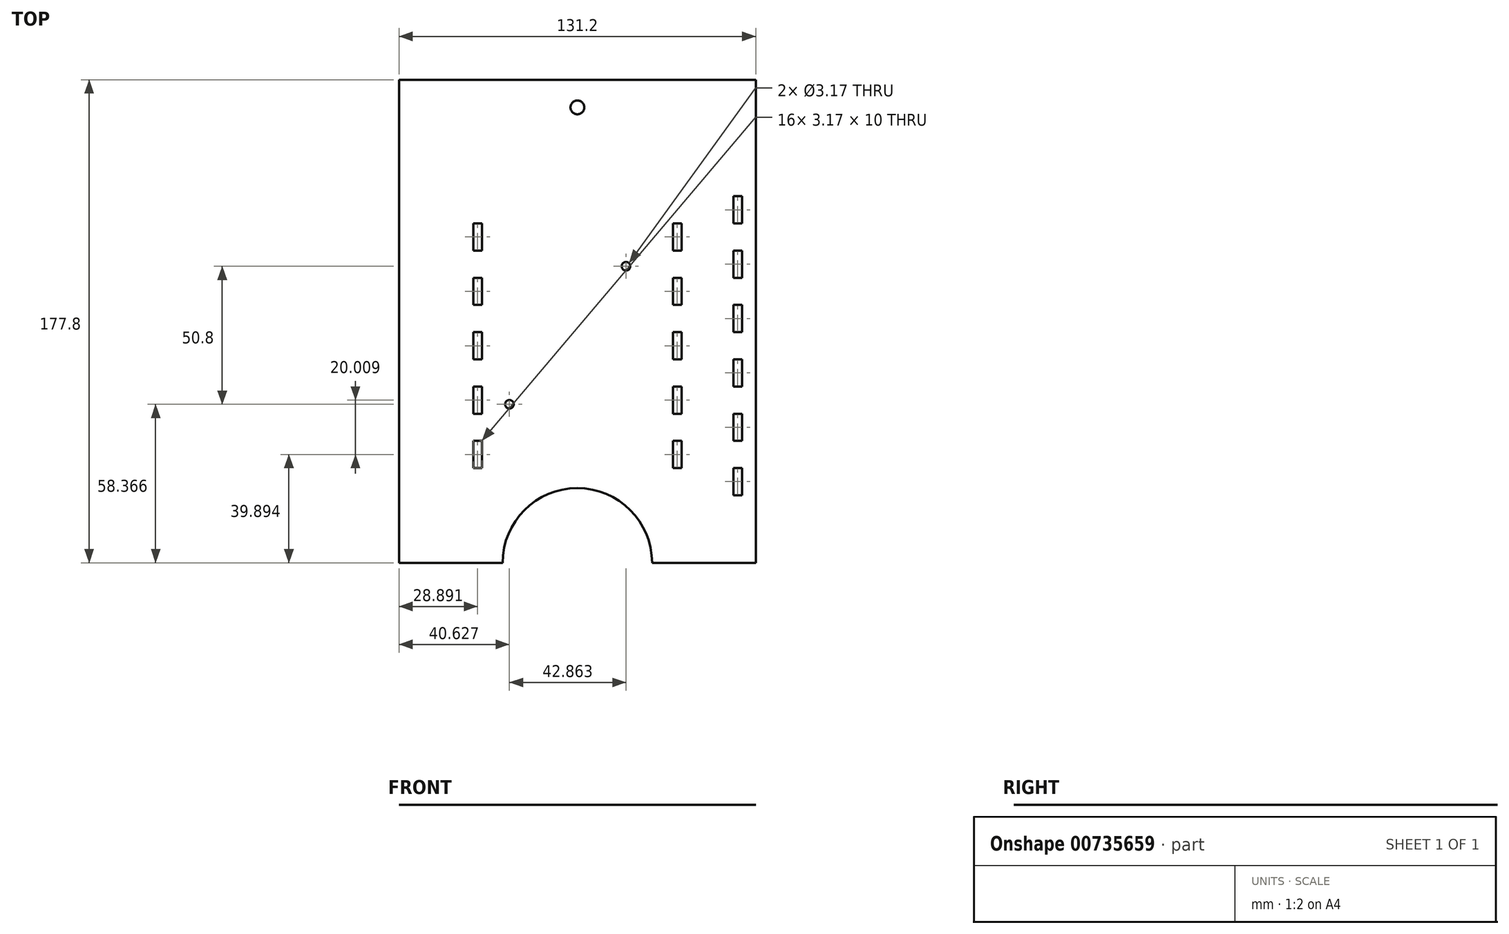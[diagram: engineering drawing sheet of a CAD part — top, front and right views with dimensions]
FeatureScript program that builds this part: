
annotation { "Feature Type Name" : "Feature", "Feature Type Description" : "" }
export const myFeature = defineFeature(function(context is Context, id is Id, definition is map)
    precondition{}
    {
        {
            var Q0;
            Q0=qCreatedBy(makeId("Top.planeOp"),FACE);
            var sketch = newSketch(context, id + "F0", { "sketchPlane" : qUnion([Q0])});
            skLineSegment(sketch, "E0.top", {"start": v(-188.86, -74.91) * mm, "end": v(-226.96, -74.91) * mm});
            skLineSegment(sketch, "E1.MirrorCS", {"start": v(-133.86, -74.91) * mm, "end": v(-95.76, -74.91) * mm});
            skCircle(sketch, "E2", {"center": v(-161.36, 92.73) * mm, "radius": 2.54 * mm});
            skLineSegment(sketch, "E3", {"start": v(-226.96, 102.89) * mm, "end": v(-95.76, 102.89) * mm});
            skArc(sketch, "E4", {"start": v(-133.86, -74.91) * mm, "mid": v(-161.36, -47.41) * mm, "end": v(-188.86, -74.91) * mm});
            skLineSegment(sketch, "E5", {"start": v(-226.96, 102.89) * mm, "end": v(-226.96, -74.91) * mm});
            skLineSegment(sketch, "E6", {"start": v(-95.76, 102.89) * mm, "end": v(-95.76, -74.91) * mm});
            skPoint(sketch, "E7", {"position": v(-221.88, 60.03) * mm});
            skPoint(sketch, "E8", {"position": v(-196.48, 60.03) * mm});
            skLineSegment(sketch, "E9.bottom", {"start": v(-221.88, 60.03) * mm, "end": v(-218.7, 60.03) * mm});
            skLineSegment(sketch, "E9.top", {"start": v(-221.88, -50.02) * mm, "end": v(-218.7, -50.02) * mm});
            skLineSegment(sketch, "E9.left", {"start": v(-221.88, 60.03) * mm, "end": v(-221.88, -50.02) * mm});
            skLineSegment(sketch, "E9.right", {"start": v(-218.7, 60.03) * mm, "end": v(-218.7, -50.02) * mm});
            skLineSegment(sketch, "E10.bottom", {"start": v(-196.48, 60.03) * mm, "end": v(-199.66, 60.03) * mm});
            skLineSegment(sketch, "E10.top", {"start": v(-196.48, -50.02) * mm, "end": v(-199.66, -50.02) * mm});
            skLineSegment(sketch, "E10.left", {"start": v(-196.48, 60.03) * mm, "end": v(-196.48, -50.02) * mm});
            skLineSegment(sketch, "E10.right", {"start": v(-199.66, 60.03) * mm, "end": v(-199.66, -50.02) * mm});
            skLineSegment(sketch, "E11.top", {"start": v(-221.88, 50.02) * mm, "end": v(-218.7, 50.02) * mm});
            skLineSegment(sketch, "E11.left", {"start": v(-221.88, 60.03) * mm, "end": v(-221.88, 50.02) * mm});
            skLineSegment(sketch, "E11.right", {"start": v(-218.7, 60.03) * mm, "end": v(-218.7, 50.02) * mm});
            skLineSegment(sketch, "E12.top", {"start": v(-221.88, 40.02) * mm, "end": v(-218.7, 40.02) * mm});
            skLineSegment(sketch, "E12.left", {"start": v(-221.88, 50.02) * mm, "end": v(-221.88, 40.02) * mm});
            skLineSegment(sketch, "E12.right", {"start": v(-218.7, 50.02) * mm, "end": v(-218.7, 40.02) * mm});
            skLineSegment(sketch, "E13.top", {"start": v(-221.88, 30.01) * mm, "end": v(-218.7, 30.01) * mm});
            skLineSegment(sketch, "E13.left", {"start": v(-221.88, 40.02) * mm, "end": v(-221.88, 30.01) * mm});
            skLineSegment(sketch, "E13.right", {"start": v(-218.7, 40.02) * mm, "end": v(-218.7, 30.01) * mm});
            skLineSegment(sketch, "E14.top", {"start": v(-221.88, 20) * mm, "end": v(-218.7, 20) * mm});
            skLineSegment(sketch, "E14.left", {"start": v(-221.88, 30.01) * mm, "end": v(-221.88, 20) * mm});
            skLineSegment(sketch, "E14.right", {"start": v(-218.7, 30.01) * mm, "end": v(-218.7, 20) * mm});
            skLineSegment(sketch, "E15.top", {"start": v(-221.88, 10) * mm, "end": v(-218.7, 10) * mm});
            skLineSegment(sketch, "E15.left", {"start": v(-221.88, 20) * mm, "end": v(-221.88, 10) * mm});
            skLineSegment(sketch, "E15.right", {"start": v(-218.7, 20) * mm, "end": v(-218.7, 10) * mm});
            skLineSegment(sketch, "E16.top", {"start": v(-221.88, 0) * mm, "end": v(-218.7, 0) * mm});
            skLineSegment(sketch, "E16.left", {"start": v(-221.88, 10) * mm, "end": v(-221.88, 0) * mm});
            skLineSegment(sketch, "E16.right", {"start": v(-218.7, 10) * mm, "end": v(-218.7, 0) * mm});
            skLineSegment(sketch, "E17.top", {"start": v(-221.88, -10) * mm, "end": v(-218.7, -10) * mm});
            skLineSegment(sketch, "E17.left", {"start": v(-221.88, 0) * mm, "end": v(-221.88, -10) * mm});
            skLineSegment(sketch, "E17.right", {"start": v(-218.7, 0) * mm, "end": v(-218.7, -10) * mm});
            skLineSegment(sketch, "E18.top", {"start": v(-221.88, -20) * mm, "end": v(-218.7, -20) * mm});
            skLineSegment(sketch, "E18.left", {"start": v(-221.88, -10) * mm, "end": v(-221.88, -20) * mm});
            skLineSegment(sketch, "E18.right", {"start": v(-218.7, -10) * mm, "end": v(-218.7, -20) * mm});
            skLineSegment(sketch, "E19.top", {"start": v(-221.88, -30.01) * mm, "end": v(-218.7, -30.01) * mm});
            skLineSegment(sketch, "E19.left", {"start": v(-221.88, -20) * mm, "end": v(-221.88, -30.01) * mm});
            skLineSegment(sketch, "E19.right", {"start": v(-218.7, -20) * mm, "end": v(-218.7, -30.01) * mm});
            skLineSegment(sketch, "E20.bottom", {"start": v(-221.88, -40.02) * mm, "end": v(-218.7, -40.02) * mm});
            skLineSegment(sketch, "E20.left", {"start": v(-221.88, -40.02) * mm, "end": v(-221.88, -50.02) * mm});
            skLineSegment(sketch, "E20.right", {"start": v(-218.7, -40.02) * mm, "end": v(-218.7, -50.02) * mm});
            skLineSegment(sketch, "E21", {"start": v(-199.66, 50.02) * mm, "end": v(-196.48, 50.02) * mm});
            skLineSegment(sketch, "E22", {"start": v(-199.66, 40.02) * mm, "end": v(-196.48, 40.02) * mm});
            skLineSegment(sketch, "E23", {"start": v(-199.66, 30.01) * mm, "end": v(-196.48, 30.01) * mm});
            skLineSegment(sketch, "E24", {"start": v(-199.66, 20) * mm, "end": v(-196.48, 20) * mm});
            skLineSegment(sketch, "E25", {"start": v(-199.66, 10) * mm, "end": v(-196.48, 10) * mm});
            skLineSegment(sketch, "E26", {"start": v(-199.66, 0) * mm, "end": v(-196.48, 0) * mm});
            skLineSegment(sketch, "E27", {"start": v(-199.66, -10) * mm, "end": v(-196.48, -10) * mm});
            skLineSegment(sketch, "E28", {"start": v(-199.66, -20) * mm, "end": v(-196.48, -20) * mm});
            skLineSegment(sketch, "E29", {"start": v(-199.66, -30.01) * mm, "end": v(-196.48, -30.01) * mm});
            skLineSegment(sketch, "E30", {"start": v(-199.66, -40.02) * mm, "end": v(-196.48, -40.02) * mm});
            skPoint(sketch, "E31", {"position": v(-161.36, 102.89) * mm});
            skLineSegment(sketch, "E32.MirrorCS", {"start": v(-104.02, 60.03) * mm, "end": v(-104.02, -50.02) * mm});
            skLineSegment(sketch, "E33.MirrorCS", {"start": v(-100.84, 60.03) * mm, "end": v(-100.84, -50.02) * mm});
            skLineSegment(sketch, "E34.MirrorCS", {"start": v(-100.84, -50.02) * mm, "end": v(-104.02, -50.02) * mm});
            skLineSegment(sketch, "E35.MirrorCS", {"start": v(-100.84, -40.02) * mm, "end": v(-104.02, -40.02) * mm});
            skLineSegment(sketch, "E36.MirrorCS", {"start": v(-100.84, -30.01) * mm, "end": v(-104.02, -30.01) * mm});
            skLineSegment(sketch, "E37.MirrorCS", {"start": v(-100.84, -20) * mm, "end": v(-104.02, -20) * mm});
            skLineSegment(sketch, "E38.MirrorCS", {"start": v(-100.84, -10) * mm, "end": v(-104.02, -10) * mm});
            skLineSegment(sketch, "E39.MirrorCS", {"start": v(-100.84, 0) * mm, "end": v(-104.02, 0) * mm});
            skLineSegment(sketch, "E40.MirrorCS", {"start": v(-100.84, 10) * mm, "end": v(-104.02, 10) * mm});
            skLineSegment(sketch, "E41.MirrorCS", {"start": v(-100.84, 20) * mm, "end": v(-104.02, 20) * mm});
            skLineSegment(sketch, "E42.MirrorCS", {"start": v(-100.84, 30.01) * mm, "end": v(-104.02, 30.01) * mm});
            skLineSegment(sketch, "E43.MirrorCS", {"start": v(-100.84, 40.02) * mm, "end": v(-104.02, 40.02) * mm});
            skLineSegment(sketch, "E44.MirrorCS", {"start": v(-100.84, 60.03) * mm, "end": v(-104.02, 60.03) * mm});
            skLineSegment(sketch, "E45.MirrorCS", {"start": v(-100.84, 50.02) * mm, "end": v(-104.02, 50.02) * mm});
            skCircle(sketch, "E46", {"center": v(-186.33, -16.54) * mm, "radius": 1.59 * mm});
            skCircle(sketch, "E47", {"center": v(-143.47, 34.26) * mm, "radius": 1.59 * mm});
            skLineSegment(sketch, "E48", {"start": v(-161.36, -74.91) * mm, "end": v(-161.36, 92.73) * mm});
            skLineSegment(sketch, "E49.MirrorCS", {"start": v(-123.07, 60.03) * mm, "end": v(-123.07, -50.02) * mm});
            skLineSegment(sketch, "E50.MirrorCS", {"start": v(-126.24, 60.03) * mm, "end": v(-126.24, -50.02) * mm});
            skLineSegment(sketch, "E51.MirrorCS", {"start": v(-126.24, 60.03) * mm, "end": v(-123.07, 60.03) * mm});
            skLineSegment(sketch, "E52.MirrorCS", {"start": v(-123.07, 40.02) * mm, "end": v(-126.24, 40.02) * mm});
            skLineSegment(sketch, "E53.MirrorCS", {"start": v(-123.07, 50.02) * mm, "end": v(-126.24, 50.02) * mm});
            skLineSegment(sketch, "E54.MirrorCS", {"start": v(-123.07, 30.01) * mm, "end": v(-126.24, 30.01) * mm});
            skLineSegment(sketch, "E55.MirrorCS", {"start": v(-123.07, 20) * mm, "end": v(-126.24, 20) * mm});
            skLineSegment(sketch, "E56.MirrorCS", {"start": v(-123.07, 10) * mm, "end": v(-126.24, 10) * mm});
            skLineSegment(sketch, "E57.MirrorCS", {"start": v(-123.07, 0) * mm, "end": v(-126.24, 0) * mm});
            skLineSegment(sketch, "E58.MirrorCS", {"start": v(-123.07, -10) * mm, "end": v(-126.24, -10) * mm});
            skLineSegment(sketch, "E59.MirrorCS", {"start": v(-123.07, -20) * mm, "end": v(-126.24, -20) * mm});
            skLineSegment(sketch, "E60.MirrorCS", {"start": v(-123.07, -30.01) * mm, "end": v(-126.24, -30.01) * mm});
            skLineSegment(sketch, "E61.MirrorCS", {"start": v(-123.07, -40.02) * mm, "end": v(-126.24, -40.02) * mm});
            skLineSegment(sketch, "E62.MirrorCS", {"start": v(-126.24, -50.02) * mm, "end": v(-123.07, -50.02) * mm});
            skSolve(sketch);
        }
        {
            var Q0;
            Q0=makeQuery(id+"F0.imprint","IMPRINT",FACE,{"disambiguationData":[TD([[makeQuery(id+"F0.imprint","IMPRINT",EDGE,{"derivedFrom":sQuery(id+"F0.wireOp",EDGE,"nGIk5Ip0-pOJQ-XxCQ-Is0m-sPOvisBLNwsg.bottom")}),-1.0]])]});
            var Q1;
            Q1=makeQuery(id+"F0.imprint","IMPRINT",FACE,{"disambiguationData":[TD([[makeQuery(id+"F0.imprint","IMPRINT",EDGE,{"derivedFrom":sQuery(id+"F0.wireOp",EDGE,"lPvULYe3-mki0-JX1R-hqT7-4afUuetgREDR.top")}),1.0]])]});
            var Q2;
            Q2=makeQuery(id+"F0.imprint","IMPRINT",FACE,{"disambiguationData":[TD([[makeQuery(id+"F0.imprint","IMPRINT",EDGE,{"derivedFrom":sQuery(id+"F0.wireOp",EDGE,"zHbGTScI-vOzz-am7E-iFKw-9wof0XKLiNPD.top")}),1.0]])]});
            var Q3;
            Q3=makeQuery(id+"F0.imprint","IMPRINT",FACE,{"disambiguationData":[TD([[makeQuery(id+"F0.imprint","IMPRINT",EDGE,{"derivedFrom":sQuery(id+"F0.wireOp",EDGE,"OLXvnb4n-Op3C-iKeX-d8kv-dKzy3YNxCHwA.bottom")}),-1.0]])]});
            var Q4;
            {var subQ0=sQuery(id+"F0.wireOp",EDGE,"E10.top");Q4=makeQuery(id+"F0.imprint","IMPRINT",FACE,{"disambiguationData":[TD([[makeQuery(id+"F0.imprint","IMPRINT",EDGE,{"derivedFrom":subQ0}),-1.0]])]});}
            var Q5;
            {var subQ0=sQuery(id+"F0.wireOp",EDGE,"E28");Q5=makeQuery(id+"F0.imprint","IMPRINT",FACE,{"disambiguationData":[TD([[makeQuery(id+"F0.imprint","IMPRINT",EDGE,{"derivedFrom":subQ0}),-1.0]])]});}
            var Q6;
            {var subQ0=sQuery(id+"F0.wireOp",EDGE,"E26");Q6=makeQuery(id+"F0.imprint","IMPRINT",FACE,{"disambiguationData":[TD([[makeQuery(id+"F0.imprint","IMPRINT",EDGE,{"derivedFrom":subQ0}),-1.0]])]});}
            var Q7;
            {var subQ0=sQuery(id+"F0.wireOp",EDGE,"E24");Q7=makeQuery(id+"F0.imprint","IMPRINT",FACE,{"disambiguationData":[TD([[makeQuery(id+"F0.imprint","IMPRINT",EDGE,{"derivedFrom":subQ0}),-1.0]])]});}
            var Q8;
            {var subQ0=sQuery(id+"F0.wireOp",EDGE,"E22");Q8=makeQuery(id+"F0.imprint","IMPRINT",FACE,{"disambiguationData":[TD([[makeQuery(id+"F0.imprint","IMPRINT",EDGE,{"derivedFrom":subQ0}),-1.0]])]});}
            var Q9;
            {var subQ0=sQuery(id+"F0.wireOp",EDGE,"E10.bottom");Q9=makeQuery(id+"F0.imprint","IMPRINT",FACE,{"disambiguationData":[TD([[makeQuery(id+"F0.imprint","IMPRINT",EDGE,{"derivedFrom":subQ0}),1.0]])]});}
            var Q10;
            Q10=makeQuery(id+"F0.imprint","IMPRINT",FACE,{"disambiguationData":[TD([[makeQuery(id+"F0.imprint","IMPRINT",EDGE,{"derivedFrom":sQuery(id+"F0.wireOp",EDGE,"E9.left")}),1.0]])]});
            var Q11;
            Q11=makeQuery(id+"F0.imprint","IMPRINT",FACE,{"disambiguationData":[TD([[makeQuery(id+"F0.imprint","IMPRINT",EDGE,{"derivedFrom":sQuery(id+"F0.wireOp",EDGE,"E17.top")}),-1.0]])]});
            var Q12;
            Q12=makeQuery(id+"F0.imprint","IMPRINT",FACE,{"disambiguationData":[TD([[makeQuery(id+"F0.imprint","IMPRINT",EDGE,{"derivedFrom":sQuery(id+"F0.wireOp",EDGE,"E15.top")}),-1.0]])]});
            var Q13;
            Q13=makeQuery(id+"F0.imprint","IMPRINT",FACE,{"disambiguationData":[TD([[makeQuery(id+"F0.imprint","IMPRINT",EDGE,{"derivedFrom":sQuery(id+"F0.wireOp",EDGE,"E13.top")}),-1.0]])]});
            var Q14;
            Q14=makeQuery(id+"F0.imprint","IMPRINT",FACE,{"disambiguationData":[TD([[makeQuery(id+"F0.imprint","IMPRINT",EDGE,{"derivedFrom":sQuery(id+"F0.wireOp",EDGE,"E11.top")}),-1.0]])]});
            var Q15;
            {var subQ2=sQuery(id+"F0.wireOp",EDGE,"09497629-de3b-43bb-86c9-92508602aed50.MirrorCS");Q15=makeQuery(id+"F0.imprint","IMPRINT",FACE,{"disambiguationData":[TD([[makeQuery(id+"F0.imprint","IMPRINT",EDGE,{"derivedFrom":subQ2}),1.0]])]});}
            var Q16;
            {var subQ0=sQuery(id+"F0.wireOp",EDGE,"7cfd7472-8029-4789-8599-c18a7f889b610.MirrorCS");Q16=makeQuery(id+"F0.imprint","IMPRINT",FACE,{"disambiguationData":[TD([[makeQuery(id+"F0.imprint","IMPRINT",EDGE,{"derivedFrom":subQ0}),1.0]])]});}
            var Q17;
            {var subQ0=sQuery(id+"F0.wireOp",EDGE,"de84e547-27da-4f0e-98cb-bd2e5754f3190.MirrorCS");Q17=makeQuery(id+"F0.imprint","IMPRINT",FACE,{"disambiguationData":[TD([[makeQuery(id+"F0.imprint","IMPRINT",EDGE,{"derivedFrom":subQ0}),1.0]])]});}
            var Q18;
            {var subQ0=sQuery(id+"F0.wireOp",EDGE,"17ab7949-a3cc-4672-9d4c-754789355df20.MirrorCS");Q18=makeQuery(id+"F0.imprint","IMPRINT",FACE,{"disambiguationData":[TD([[makeQuery(id+"F0.imprint","IMPRINT",EDGE,{"derivedFrom":subQ0}),-1.0]])]});}
            var Q19;
            {var subQ0=sQuery(id+"F0.wireOp",EDGE,"6a559047-fd53-4c68-a663-3248d341b3a90.MirrorCS");Q19=makeQuery(id+"F0.imprint","IMPRINT",FACE,{"disambiguationData":[TD([[makeQuery(id+"F0.imprint","IMPRINT",EDGE,{"derivedFrom":subQ0}),1.0]])]});}
            var Q20;
            {var subQ0=sQuery(id+"F0.wireOp",EDGE,"973d1edd-eca4-44a4-bda7-f025a22b30910.MirrorCS");Q20=makeQuery(id+"F0.imprint","IMPRINT",FACE,{"disambiguationData":[TD([[makeQuery(id+"F0.imprint","IMPRINT",EDGE,{"derivedFrom":subQ0}),-1.0]])]});}
            var Q21;
            {var subQ0=sQuery(id+"F0.wireOp",EDGE,"E43.MirrorCS");Q21=makeQuery(id+"F0.imprint","IMPRINT",FACE,{"disambiguationData":[TD([[makeQuery(id+"F0.imprint","IMPRINT",EDGE,{"derivedFrom":subQ0}),-1.0]])]});}
            var Q22;
            {var subQ0=sQuery(id+"F0.wireOp",EDGE,"E41.MirrorCS");Q22=makeQuery(id+"F0.imprint","IMPRINT",FACE,{"disambiguationData":[TD([[makeQuery(id+"F0.imprint","IMPRINT",EDGE,{"derivedFrom":subQ0}),-1.0]])]});}
            var Q23;
            {var subQ0=sQuery(id+"F0.wireOp",EDGE,"E39.MirrorCS");Q23=makeQuery(id+"F0.imprint","IMPRINT",FACE,{"disambiguationData":[TD([[makeQuery(id+"F0.imprint","IMPRINT",EDGE,{"derivedFrom":subQ0}),-1.0]])]});}
            var Q24;
            {var subQ0=sQuery(id+"F0.wireOp",EDGE,"E37.MirrorCS");Q24=makeQuery(id+"F0.imprint","IMPRINT",FACE,{"disambiguationData":[TD([[makeQuery(id+"F0.imprint","IMPRINT",EDGE,{"derivedFrom":subQ0}),-1.0]])]});}
            var Q25;
            {var subQ0=sQuery(id+"F0.wireOp",EDGE,"E35.MirrorCS");Q25=makeQuery(id+"F0.imprint","IMPRINT",FACE,{"disambiguationData":[TD([[makeQuery(id+"F0.imprint","IMPRINT",EDGE,{"derivedFrom":subQ0}),-1.0]])]});}
            var Q26;
            {var subQ0=sQuery(id+"F0.wireOp",EDGE,"E51.MirrorCS");Q26=makeQuery(id+"F0.imprint","IMPRINT",FACE,{"disambiguationData":[TD([[makeQuery(id+"F0.imprint","IMPRINT",EDGE,{"derivedFrom":subQ0}),-1.0]])]});}
            var Q27;
            {var subQ0=sQuery(id+"F0.wireOp",EDGE,"E52.MirrorCS");Q27=makeQuery(id+"F0.imprint","IMPRINT",FACE,{"disambiguationData":[TD([[makeQuery(id+"F0.imprint","IMPRINT",EDGE,{"derivedFrom":subQ0}),1.0]])]});}
            var Q28;
            {var subQ0=sQuery(id+"F0.wireOp",EDGE,"E55.MirrorCS");Q28=makeQuery(id+"F0.imprint","IMPRINT",FACE,{"disambiguationData":[TD([[makeQuery(id+"F0.imprint","IMPRINT",EDGE,{"derivedFrom":subQ0}),1.0]])]});}
            var Q29;
            {var subQ0=sQuery(id+"F0.wireOp",EDGE,"E57.MirrorCS");Q29=makeQuery(id+"F0.imprint","IMPRINT",FACE,{"disambiguationData":[TD([[makeQuery(id+"F0.imprint","IMPRINT",EDGE,{"derivedFrom":subQ0}),1.0]])]});}
            var Q30;
            {var subQ0=sQuery(id+"F0.wireOp",EDGE,"E59.MirrorCS");Q30=makeQuery(id+"F0.imprint","IMPRINT",FACE,{"disambiguationData":[TD([[makeQuery(id+"F0.imprint","IMPRINT",EDGE,{"derivedFrom":subQ0}),1.0]])]});}
            var Q31;
            {var subQ2=sQuery(id+"F0.wireOp",EDGE,"E61.MirrorCS");Q31=makeQuery(id+"F0.imprint","IMPRINT",FACE,{"disambiguationData":[TD([[makeQuery(id+"F0.imprint","IMPRINT",EDGE,{"derivedFrom":subQ2}),1.0]])]});}
            var Q32;
            {var subQ76=sQuery(id+"F0.wireOp",EDGE,"E0.top");Q32=makeQuery(id+"F0.imprint","IMPRINT",FACE,{"disambiguationData":[TD([[makeQuery(id+"F0.imprint","IMPRINT",EDGE,{"derivedFrom":subQ76}),-1.0]])]});}
            extrude(context, id + "F1", {"entities" : qUnion([Q0, Q1, Q2, Q3, Q4, Q5, Q6, Q7, Q8, Q9, Q10, Q11, Q12, Q13, Q14, Q15, Q16, Q17, Q18, Q19, Q20, Q21, Q22, Q23, Q24, Q25, Q26, Q27, Q28, Q29, Q30, Q31, Q32]), "depth" : 1 / 203.2 * mm, "offsetDistance" : 25.4 * mm});
        }
    });
